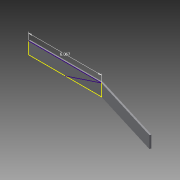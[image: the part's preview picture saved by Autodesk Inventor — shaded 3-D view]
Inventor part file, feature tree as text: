
AUTODESK INVENTOR PART (.ipt)
format: ipt  version: 2013 (Build 170138000, 138)  size: 97,280 bytes
history: native  units: in
note: dims shown in document units (in); Inventor stores cm internally (conversion verified against a paired STEP export)
features: sheet_metal_op x4, sketch x3, other x2
ambient origin geometry x8: Origin, YZ Plane, XZ Plane, XY Plane, X Axis, Y Axis, Z Axis, Center Point
bodies: Solid1 (feature_tree)
feature tree (9):
  sheet_metal_op  "Face1"
  sketch  "Sketch2"  dims[d1=1.0in]
  sheet_metal_op  "Flange1"
  sketch  "Sketch1"  dims[d0=6.067in]
  other  "Plate1"
  sketch  "Sketch3"  dims[d2=0.125in d3=6.067in d4=0.125in d5=0.0625in d6=0.25in d7=0.125in d8=6.067in d9=0.1172in d10=0.05in d11=0.5in d12=0.125in d13=0.125in]
  other  "Plate2"
  sheet_metal_op  "Bend1"
  sheet_metal_op  "Corner1"
